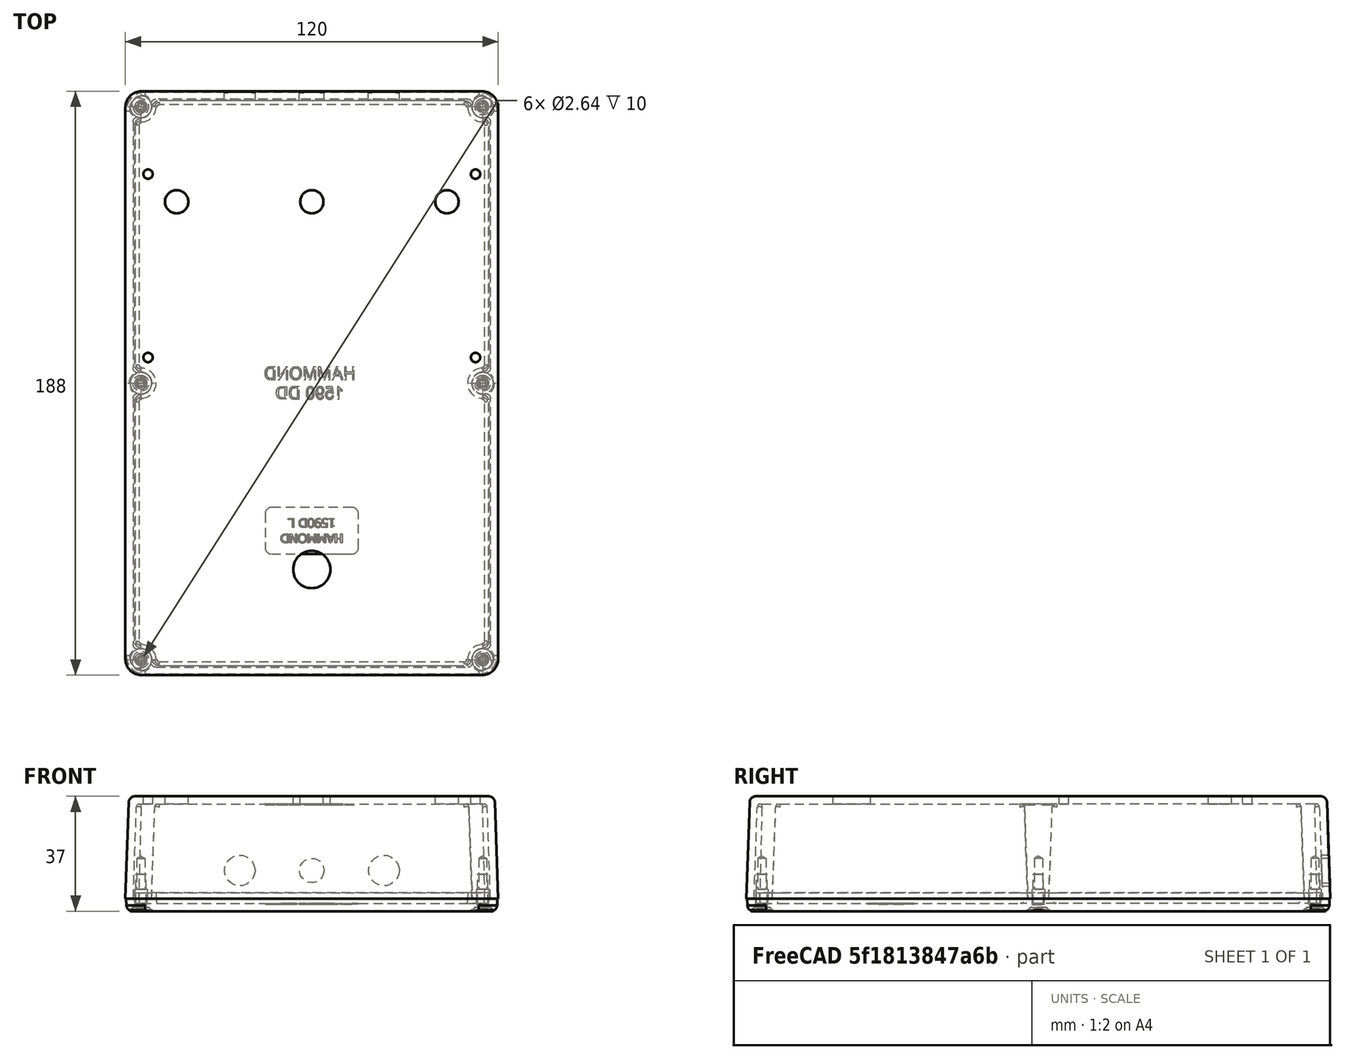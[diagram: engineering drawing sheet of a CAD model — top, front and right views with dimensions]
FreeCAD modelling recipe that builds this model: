
FCSTD DOCUMENT  (FreeCAD 0.18R16131 (Git))
Label: #700-000-A - Enclosure [1590DD, Portrait] - STEP VRML
License: All rights reserved
LicenseURL: http://en.wikipedia.org/wiki/All_rights_reserved
objects: Part::Cylinder×11, PartDesign::ShapeBinder×9, Part::Feature×8, PartDesign::Plane×5, App::Part×5, Part::MultiFuse×2, App::VRMLObject×2, PartDesign::Body×1, Part::Cut×1
note: 37 computed .brp shape members not serialized (recipe doc carries the construction recipe); baked Part::Feature solids carry a one-line shape summary decoded from their .brp

FEATURE [PartDesign::Plane] DatumPlane  label="Origin_XY_DatumPlane"
  AttachmentOffset = pos=(-75,-100,0) rot=(0,0,1;0rad)
  Length = 104.339
  MapMode = 5
  Placement = pos=(-75,-100,0) rot=(0,0,1;0rad)
  ResizeMode = 1
  Support = -> [XY_Plane001]
  Width = 200
FEATURE [Part::Feature] Part__Feature  label="#700-001 - 1590DD Box"
  Placement = pos=(0,0,0) rot=(0.707107,0.707107,0;3.14159rad)
  shape: bbox 120 x 188 x 451.1 mm, 273 faces (baked)
FEATURE [Part::Feature] Part__Feature001  label="#700-001 - 1590DD - Lid"
  Placement = pos=(0,0,0) rot=(0,0.707107,0.707107;3.14159rad)
  shape: bbox 187.5 x 5.937 x 119.5 mm, 345 faces (baked)
FEATURE [Part::Feature] Part__Feature002  label="#700-001 - 1590DD - Screw 4/6"
  Placement = pos=(1.2e-14,1.5362,-55) rot=(0,1,0;0.650238rad)
  shape: bbox 6.871 x 11.85 x 6.871 mm, 25 faces (baked)
FEATURE [Part::Feature] Part__Feature003  label="#700-001 - 1590DD - Screw 2/6"
  Placement = pos=(-1.2e-14,1.5362,55) rot=(0,1,0;0.650238rad)
  shape: bbox 6.871 x 11.85 x 6.871 mm, 25 faces (baked)
FEATURE [Part::Feature] Part__Feature004  label="#700-001 - 1590DD - Screw 1/6"
  Placement = pos=(-89,1.5362,55) rot=(0,1,0;0.650238rad)
  shape: bbox 6.871 x 11.85 x 6.871 mm, 25 faces (baked)
FEATURE [Part::Feature] Part__Feature005  label="#700-001 - 1590DD - Screw 3/6"
  Placement = pos=(-89,1.5362,-55) rot=(0,-1,0;0.529817rad)
  shape: bbox 6.871 x 11.85 x 6.871 mm, 25 faces (baked)
FEATURE [Part::Feature] Part__Feature006  label="#700-001 - 1590DD - Screw 5/6"
  Placement = pos=(89,1.5362,55) rot=(0,0,1;0rad)
  shape: bbox 6.871 x 11.85 x 6.871 mm, 25 faces (baked)
FEATURE [Part::Feature] Part__Feature007  label="#700-001 - 1590DD - Screw 6/6"
  Placement = pos=(89,1.5362,-55) rot=(0,0,1;0rad)
  shape: bbox 6.871 x 11.85 x 6.871 mm, 25 faces (baked)
FEATURE [Part::MultiFuse] Fusion  label="#700-000 - Enclosure - Lid & Screws, Fusion"
  Placement = pos=(0,0,0) rot=(0.57735,-0.57735,0.57735;4.18879rad)
  Shapes = -> [Part__Feature001,Part__Feature004,Part__Feature003,Part__Feature005,Part__Feature002,Part__Feature006,Part__Feature007]
FEATURE [Part::Cylinder] Cylinder  label="Drill - Potentiometer - Rate [D=7.5, X=-43.5, Y=58.42]"
  Angle = 360
  AttacherType = Attacher::AttachEngine3D
  Height = 10
  Placement = pos=(-43.498,58.42,25) rot=(0,0,1;0rad)
  Radius = 3.75
FEATURE [Part::Cylinder] Cylinder001  label="Drill - Potentiometer - Depth [D7.5, X=0.0, Y = 58.42]]"
  Angle = 360
  AttacherType = Attacher::AttachEngine3D
  Height = 10
  Placement = pos=(0,58.42,25) rot=(0,0,1;0rad)
  Radius = 3.75
FEATURE [Part::Cylinder] Cylinder002  label="Drill - Potentiometer - Feedback [D=7.5, X=43.5, Y=58.42]"
  Angle = 360
  AttacherType = Attacher::AttachEngine3D
  Height = 10
  Placement = pos=(43.498,58.42,25) rot=(0,0,1;0rad)
  Radius = 3.75
FEATURE [PartDesign::Plane] DatumPlane001  label="Enclosure_Face_XY_DatumPlane"
  Length = 24
  MapMode = 5
  Placement = pos=(0,0,30.5) rot=(1,0,0;3.14159rad)
  ResizeMode = 0
  Width = 24
FEATURE [Part::Cylinder] Cylinder003  label="Drill - Standoff 4/4 [D=3.0, X=-52.705, Y=8.26]"
  Angle = 360
  AttacherType = Attacher::AttachEngine3D
  Height = 10
  Placement = pos=(-52.705,8.26,26) rot=(0,0,1;0rad)
  Radius = 1.5
FEATURE [Part::Cylinder] Cylinder004  label="Drill - Standoff 3/4 [D=3.0, X=52.705, Y=8.26]"
  Angle = 360
  AttacherType = Attacher::AttachEngine3D
  Height = 10
  Placement = pos=(52.705,8.26,26) rot=(0,0,1;0rad)
  Radius = 1.5
FEATURE [Part::Cylinder] Cylinder005  label="Drill - Standoff 2/4 [D=3.0, X=-52.705, Y=67.31]"
  Angle = 360
  AttacherType = Attacher::AttachEngine3D
  Height = 10
  Placement = pos=(-52.705,67.31,26) rot=(0,0,1;0rad)
  Radius = 1.5
FEATURE [Part::Cylinder] Cylinder006  label="Drill - Standoff 1/4 [D=3.0, X=52.705, Y=67.31]"
  Angle = 360
  AttacherType = Attacher::AttachEngine3D
  Height = 10
  Placement = pos=(52.705,67.31,26) rot=(0,0,1;0rad)
  Radius = 1.5
FEATURE [App::Part] Part001  label="#700-000 - Enclosure - Lid & Screws"
  Group = -> [Part__Feature004,Part__Feature007,Part__Feature005,Part__Feature001,Part__Feature003,Part__Feature006,Part__Feature002,Fusion]
  Origin = -> Origin002
  Placement = pos=(0,0,0) rot=(0,0,1;3.14159rad)
FEATURE [PartDesign::ShapeBinder] ShapeBinder  label="Enclosure_Lid_Inside"
  Placement = pos=(0,0,0) rot=(0.707107,0.707107,0;3.14159rad)
  Support = -> [Fusion]
  TraceSupport = false
FEATURE [PartDesign::ShapeBinder] ShapeBinder001  label="Enclosure_Lid_Lip"
  Placement = pos=(0,0,0) rot=(0.707107,0.707107,0;3.14159rad)
  Support = -> [Fusion]
  TraceSupport = false
FEATURE [PartDesign::ShapeBinder] ShapeBinder002  label="Enclosure_Lid_Outside"
  Placement = pos=(0,0,0) rot=(0.707107,0.707107,0;3.14159rad)
  Support = -> [Fusion]
  TraceSupport = false
FEATURE [PartDesign::ShapeBinder] ShapeBinder003  label="Enclosure_Box_Top_Outside"
  Placement = pos=(0,0,0) rot=(0.707107,0.707107,0;3.14159rad)
  Support = -> [Part__Feature]
  TraceSupport = false
FEATURE [PartDesign::ShapeBinder] ShapeBinder004  label="Enclosure_Box_Top_Inside"
  Placement = pos=(0,0,0) rot=(0.707107,0.707107,0;3.14159rad)
  Support = -> [Part__Feature]
  TraceSupport = false
FEATURE [PartDesign::ShapeBinder] ShapeBinder005  label="Enclosure_Box_Rear_Outside"
  Placement = pos=(0,0,0) rot=(0.707107,0.707107,0;3.14159rad)
  Support = -> [Part__Feature]
  TraceSupport = false
FEATURE [PartDesign::ShapeBinder] ShapeBinder006  label="Enclosure_Box_Rear_Inside"
  Placement = pos=(0,0,0) rot=(0.707107,0.707107,0;3.14159rad)
  Support = -> [Part__Feature]
  TraceSupport = false
FEATURE [PartDesign::ShapeBinder] ShapeBinder007  label="Enclosure_Box_Front_Outside"
  Placement = pos=(0,0,0) rot=(0.707107,0.707107,0;3.14159rad)
  Support = -> [Part__Feature]
  TraceSupport = false
FEATURE [PartDesign::ShapeBinder] ShapeBinder008  label="Enclosure_Box_Front_Inside"
  Placement = pos=(0,0,0) rot=(0.707107,0.707107,0;3.14159rad)
  Support = -> [Part__Feature]
  TraceSupport = false
FEATURE [Part::Cylinder] Cylinder007  label="Drill - Audio Jack 1/2 [D=10.0, X=-23.2, Z=9.1]"
  Angle = 360
  AttacherType = Attacher::AttachEngine3D
  Height = 10
  Placement = pos=(-23.2,90,9.1) rot=(-1,0,0;1.5708rad)
  Radius = 5
  expr: Placement.Base.z = 1 + 1.6 + 6.5
FEATURE [Part::Cylinder] Cylinder008  label="Drill - Audio Jack 2/2 [D=10.0, X=23.2, Z=9.1]"
  Angle = 360
  AttacherType = Attacher::AttachEngine3D
  Height = 10
  Placement = pos=(23.2,90,9.1) rot=(-1,0,0;1.5708rad)
  Radius = 5
  expr: Placement.Base.z = 1 + 1.6 + 6.5
FEATURE [Part::Cylinder] Cylinder009  label="Drill - Power Jack [D=8.0, X=0.0, Y=9.1]"
  Angle = 360
  AttacherType = Attacher::AttachEngine3D
  Height = 10
  Placement = pos=(0,90,9.1) rot=(-1,0,0;1.5708rad)
  Radius = 4
FEATURE [PartDesign::Plane] DatumPlane002  label="DatumPlane_Rear_Inside"
  Length = 24.068
  MapMode = 5
  Placement = pos=(2.03e-14,91.387,3.19131) rot=(0,0.71934,-0.694658;3.14159rad)
  ResizeMode = 0
  Support = -> [ShapeBinder006]
  Width = 24.7538
FEATURE [PartDesign::Plane] DatumPlane003  label="DatumPlane_Top_Inside"
  Length = 24
  MapMode = 5
  Placement = pos=(0,0,30.5) rot=(0.707107,0.707107,0;3.14159rad)
  ResizeMode = 0
  Support = -> [ShapeBinder004]
  Width = 24
FEATURE [PartDesign::Plane] DatumPlane004  label="DatumPlane_Lid_Inside"
  Length = 24
  MapMode = 5
  Placement = pos=(0,0,-1.5) rot=(0,0,1;1.5708rad)
  ResizeMode = 0
  Support = -> [ShapeBinder]
  Width = 24
FEATURE [PartDesign::Body] Body  label="Datum References"
  Group = -> [DatumPlane,DatumPlane001,ShapeBinder,ShapeBinder001,ShapeBinder002,ShapeBinder003,ShapeBinder004,ShapeBinder005,ShapeBinder006,ShapeBinder007,ShapeBinder008,DatumPlane002,DatumPlane003,DatumPlane004]
  Origin = -> Origin001
FEATURE [App::Part] Part003  label="#700-000 - Datum References"
  Group = -> [Body]
  Origin = -> Origin004
FEATURE [Part::Cylinder] Cylinder010  label="Drill - Footswitch [D=12.0, X=0.0, Y=-60.0]"
  Angle = 360
  AttacherType = Attacher::AttachEngine3D
  Height = 10
  Placement = pos=(0,-60,25) rot=(0,0,1;0rad)
  Radius = 6
FEATURE [Part::MultiFuse] Fusion001  label="Drills"
  Shapes = -> [Cylinder,Cylinder002,Cylinder001,Cylinder003,Cylinder004,Cylinder005,Cylinder006,Cylinder007,Cylinder008,Cylinder009,Cylinder010]
FEATURE [Part::Cut] Cut  label="#700-000 - Enclosure - Box, Drilled"
  Base = -> Part__Feature
  Tool = -> Fusion001
FEATURE [App::Part] Part002  label="#700-000 - Enclosure - Box, Machined"
  Group = -> [Part__Feature,Fusion001,Cylinder002,Cylinder006,Cylinder004,Cylinder005,Cylinder,Cylinder001,Cylinder003,Cut]
  Origin = -> Origin003
FEATURE [App::Part] Part  label="#700-000-A - Enclosure [1590DD, Portrait] - STEP"
  Group = -> [Part001,Part002,Part003]
  Origin = -> Origin
FEATURE [App::VRMLObject] _700_000_A___Enclosure___Box__1590DD__Portrait_  label="#700-000-A - Enclosure - Box [1590DD, Portrait]"
FEATURE [App::VRMLObject] _700_000_A___Enclosure___Lid__1590DD__Portrait_  label="#700-000-A - Enclosure - Lid [1590DD, Portrait]"
FEATURE [App::Part] Part004  label="#700-000-A - Enclosure [1590DD, Portrait] - VRML"
  Group = -> [_700_000_A___Enclosure___Box__1590DD__Portrait_,_700_000_A___Enclosure___Lid__1590DD__Portrait_]
  Origin = -> Origin005
